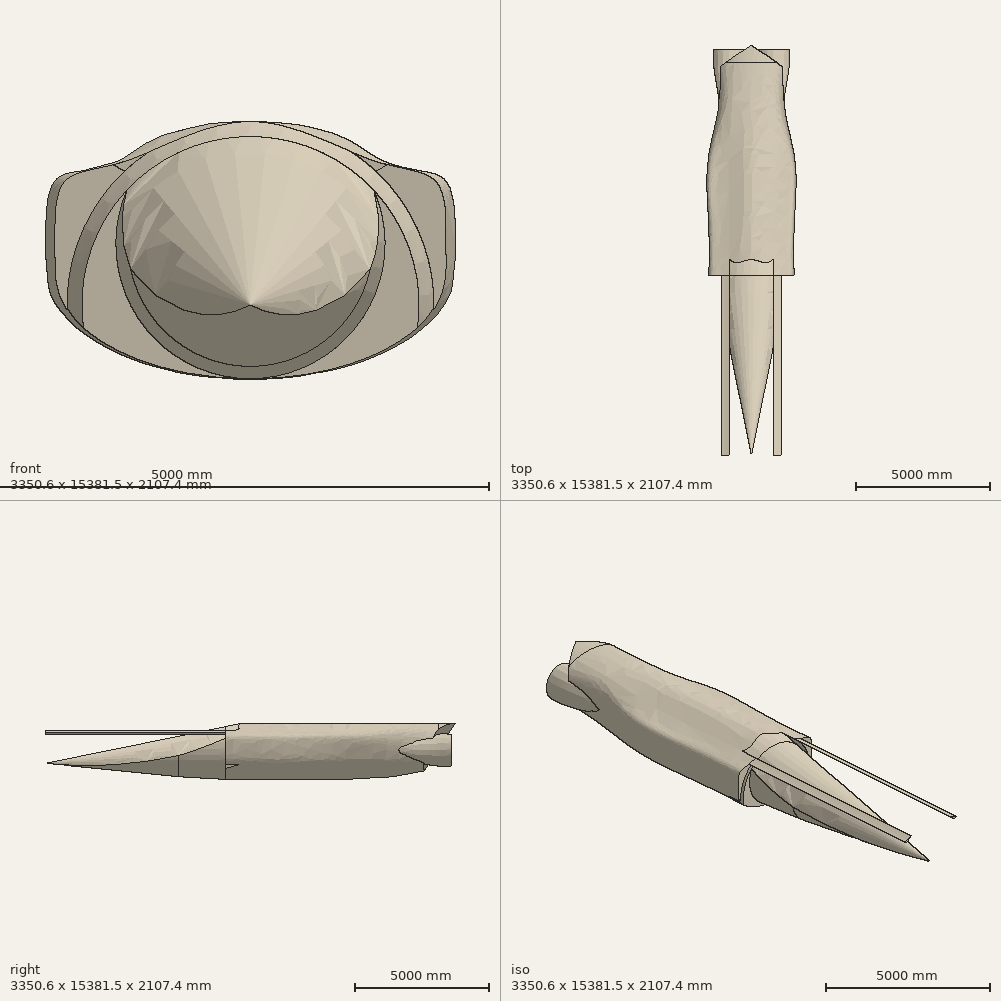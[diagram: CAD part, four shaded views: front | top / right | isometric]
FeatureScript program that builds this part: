
annotation { "Feature Type Name" : "Feature", "Feature Type Description" : "" }
export const myFeature = defineFeature(function(context is Context, id is Id, definition is map)
    precondition{}
    {
        {
            var Q0;
            Q0=qCreatedBy(makeId("Front.planeOp"),FACE);
            cPlane(context, id + "F0", {"entities" : qUnion([Q0]), "cplaneType" : CPlaneType.OFFSET, "offset" : 1750 * mm, "width" : 152.4 * mm, "height" : 152.4 * mm});
        }
        {
            var Q0;
            Q0=qCreatedBy(id+"F0.planeOp",FACE);
            var sketch = newSketch(context, id + "F1", { "sketchPlane" : qUnion([Q0])});
            skPoint(sketch, "E0.middle", {"position": v(0, 0) * mm});
            skFitSpline(sketch, "E1", {"points": [v(0, 1000) * mm, v(1060, 662.5) * mm, v(1517.6, 506.84) * mm, v(1600, 0) * mm, v(1517.6, -506.84) * mm, v(750, -1000) * mm, v(-750, -1000) * mm, v(-1517.6, -506.84) * mm, v(-1600, 0) * mm, v(-1517.6, 506.84) * mm, v(-1060, 662.5) * mm, v(0, 1000) * mm]});
            skSolve(sketch);
        }
        {
            var Q0;
            Q0=qCreatedBy(makeId("Front.planeOp"),FACE);
            var sketch = newSketch(context, id + "F2", { "sketchPlane" : qUnion([Q0])});
            skPoint(sketch, "E2.middle", {"position": v(0, 0) * mm});
            skFitSpline(sketch, "E3", {"points": [v(0, 1000) * mm, v(1060, 662.5) * mm, v(1517.6, 506.84) * mm, v(1600, 0) * mm, v(1517.6, -506.84) * mm, v(750, -1000) * mm, v(-750, -1000) * mm, v(-1517.6, -506.84) * mm, v(-1600, 0) * mm, v(-1517.6, 506.84) * mm, v(-1060, 662.5) * mm, v(0, 1000) * mm]});
            skSolve(sketch);
        }
        {
            var Q0;
            Q0=qCreatedBy(makeId("Front.planeOp"),FACE);
            cPlane(context, id + "F3", {"entities" : qUnion([Q0]), "cplaneType" : CPlaneType.OFFSET, "offset" : 2800 * mm, "oppositeDirection" : true, "width" : 150 * mm, "height" : 150 * mm});
        }
        {
            var Q0;
            Q0=qCreatedBy(id+"F3.planeOp",FACE);
            var sketch = newSketch(context, id + "F4", { "sketchPlane" : qUnion([Q0])});
            skPoint(sketch, "E4.middle", {"position": v(0, 0) * mm});
            skFitSpline(sketch, "E5", {"points": [v(0, 1000) * mm, v(1060, 662.5) * mm, v(1517.6, 506.84) * mm, v(1600, 0) * mm, v(1517.6, -506.84) * mm, v(750, -1000) * mm, v(-750, -1000) * mm, v(-1517.6, -506.84) * mm, v(-1600, 0) * mm, v(-1517.6, 506.84) * mm, v(-1060, 662.5) * mm, v(0, 1000) * mm]});
            skSolve(sketch);
        }
        {
            var Q0;
            Q0=qCreatedBy(makeId("Front.planeOp"),FACE);
            cPlane(context, id + "F5", {"entities" : qUnion([Q0]), "cplaneType" : CPlaneType.OFFSET, "offset" : 4500 * mm, "oppositeDirection" : true, "width" : 150 * mm, "height" : 150 * mm});
        }
        {
            var Q0;
            Q0=qCreatedBy(id+"F5.planeOp",FACE);
            var sketch = newSketch(context, id + "F6", { "sketchPlane" : qUnion([Q0])});
            skPoint(sketch, "E6.middle", {"position": v(0, 0) * mm});
            skFitSpline(sketch, "E7", {"points": [v(0, 1000) * mm, v(1060, 662.5) * mm, v(1250, 0) * mm, v(1060, -662.5) * mm, v(0, -1000) * mm, v(-1060, -662.5) * mm, v(-1250, 0) * mm, v(-1060, 662.5) * mm, v(0, 1000) * mm]});
            skSolve(sketch);
        }
        {
            var Q0;
            Q0=qCreatedBy(makeId("Front.planeOp"),FACE);
            cPlane(context, id + "F7", {"entities" : qUnion([Q0]), "cplaneType" : CPlaneType.OFFSET, "offset" : 6232.05 * mm, "oppositeDirection" : true, "width" : 150 * mm, "height" : 150 * mm});
        }
        {
            var Q0;
            Q0=qCreatedBy(id+"F7.planeOp",FACE);
            var sketch = newSketch(context, id + "F8", { "sketchPlane" : qUnion([Q0])});
            skPoint(sketch, "E8.middle", {"position": v(0, 0) * mm});
            skFitSpline(sketch, "E9", {"points": [v(0, 1000) * mm, v(1060, 662.5) * mm, v(1250, 0) * mm, v(848, -530) * mm, v(-848, -530) * mm, v(-1250, 0) * mm, v(-1060, 662.5) * mm, v(0, 1000) * mm]});
            skSolve(sketch);
        }
        {
            var Q0;
            Q0=qSketchRegion(id+"F1",true);
            var Q1;
            Q1=qSketchRegion(id+"F2",true);
            var Q2;
            Q2=qSketchRegion(id+"F4",true);
            var Q3;
            Q3=qSketchRegion(id+"F6",true);
            var Q4;
            Q4=qSketchRegion(id+"F8",true);
            loft(context, id + "F9", {"sheetProfilesArray" : [{ "sheetProfileEntities" : qUnion([Q0]) }, { "sheetProfileEntities" : qUnion([Q1]) }, { "sheetProfileEntities" : qUnion([Q2]) }, { "sheetProfileEntities" : qUnion([Q3]) }, { "sheetProfileEntities" : qUnion([Q4]) }]});
        }
        {
            var Q0;
            Q0=makeQuery(id+"F9.opLoft","CAP_FACE",FACE,{"disambiguationData":[OSD([makeQuery(id+"F8.imprint","IMPRINT",FACE,{"disambiguationData":[TD([[makeQuery(id+"F8.imprint","IMPRINT",EDGE,{"derivedFrom":sQuery(id+"F8.wireOp",EDGE,"E9")}),-1.0]])]})])],"isStart":true});
            extrude(context, id + "F10", {"entities" : qUnion([Q0]), "operationType" : NewBodyOperationType.ADD, "depth" : 649.4 * mm});
        }
        {
            var Q0;
            Q0=qCreatedBy(makeId("Right.planeOp"),FACE);
            var sketch = newSketch(context, id + "F11", { "sketchPlane" : qUnion([Q0])});
            skLineSegment(sketch, "E10", {"start": v(0, 0) * mm, "end": v(4500, 0) * mm});
            skLineSegment(sketch, "E11", {"start": v(4500, 0) * mm, "end": v(6232.05, 0) * mm});
            skLineSegment(sketch, "E12", {"start": v(4500, 0) * mm, "end": v(4500, 1000) * mm});
            skLineSegment(sketch, "E13", {"start": v(4500, 1000) * mm, "end": v(6881.46, 1000) * mm});
            skLineSegment(sketch, "E14", {"start": v(6881.46, 1000) * mm, "end": v(6881.46, -1000) * mm});
            skLineSegment(sketch, "E15", {"start": v(6881.46, 1000) * mm, "end": v(6232.05, 0) * mm});
            skLineSegment(sketch, "E16", {"start": v(6232.05, 0) * mm, "end": v(5582.64, -1000) * mm});
            skLineSegment(sketch, "E17", {"start": v(5582.64, -1000) * mm, "end": v(6881.46, -1000) * mm});
            skSolve(sketch);
        }
        {
            var Q0;
            Q0=makeQuery(id+"F11.imprint","IMPRINT",FACE,{"disambiguationData":[TD([[makeQuery(id+"F11.imprint","IMPRINT",EDGE,{"derivedFrom":sQuery(id+"F11.wireOp",EDGE,"E14")}),-1.0]])]});
            var Q1;
            Q1=sQuery(id+"F11.wireOp",EDGE,"E13");
            revolve(context, id + "F12", {"operationType" : NewBodyOperationType.REMOVE, "entities" : qUnion([Q0]), "axis" : qUnion([Q1]), "revolveType" : RevolveType.SYMMETRIC, "oppositeDirection" : true, "angle" : 182 * degree});
        }
        {
            var Q0;
            Q0=makeQuery(id+"F9.opLoft","CAP_FACE",FACE,{"disambiguationData":[OSD([makeQuery(id+"F1.imprint","IMPRINT",FACE,{"disambiguationData":[TD([[makeQuery(id+"F1.imprint","IMPRINT",EDGE,{"derivedFrom":sQuery(id+"F1.wireOp",EDGE,"E1")}),-1.0]])]})])],"isStart":true});
            extrude(context, id + "F13", {"entities" : qUnion([Q0]), "depth" : 6750 * mm});
        }
        {
            var Q0;
            Q0=qCreatedBy(makeId("Right.planeOp"),FACE);
            var sketch = newSketch(context, id + "F14", { "sketchPlane" : qUnion([Q0])});
            skLineSegment(sketch, "E18", {"start": v(0, 0) * mm, "end": v(-3500, 0) * mm});
            skLineSegment(sketch, "E19", {"start": v(-3500, 0) * mm, "end": v(-3500, -1000) * mm});
            skLineSegment(sketch, "E20", {"start": v(-3500, -1000) * mm, "end": v(-8500, -1000) * mm});
            skLineSegment(sketch, "E21", {"start": v(-8500, -1000) * mm, "end": v(-8500, -499.31) * mm});
            skLineSegment(sketch, "E22", {"start": v(-1151.4, 0) * mm, "end": v(-1151.4, 1000) * mm});
            skLineSegment(sketch, "E23", {"start": v(-1151.4, 1000) * mm, "end": v(-8500, -499.31) * mm});
            skLineSegment(sketch, "E24", {"start": v(-8500, -499.31) * mm, "end": v(-3500, -1000) * mm});
            skLineSegment(sketch, "E25", {"start": v(-1151.4, 1000) * mm, "end": v(-8500, 1000) * mm});
            skLineSegment(sketch, "E26", {"start": v(-8500, 1000) * mm, "end": v(-8500, -499.31) * mm});
            skLineSegment(sketch, "E27", {"start": v(-8500, -1000) * mm, "end": v(-8500, -1750) * mm});
            skLineSegment(sketch, "E28", {"start": v(-8500, -1750) * mm, "end": v(-1750, -1750) * mm});
            skPoint(sketch, "E28.endSnap0", {"position": v(-1750, 0) * mm});
            skLineSegment(sketch, "E29", {"start": v(-1750, 0) * mm, "end": v(-1750, -1099.92) * mm});
            skLineSegment(sketch, "E30", {"start": v(-1750, -1099.92) * mm, "end": v(-3500, -1000) * mm});
            skLineSegment(sketch, "E31", {"start": v(-1750, -1099.92) * mm, "end": v(-1750, -1750) * mm});
            skLineSegment(sketch, "E32", {"start": v(-8500, -499.31) * mm, "end": v(-3500, -499.31) * mm});
            skSolve(sketch);
        }
        {
            var Q0;
            Q0=makeQuery(id+"F14.imprint","IMPRINT",FACE,{"disambiguationData":[TD([[makeQuery(id+"F14.imprint","IMPRINT",EDGE,{"derivedFrom":sQuery(id+"F14.wireOp",EDGE,"E23")}),-1.0]])]});
            var Q1;
            Q1=sQuery(id+"F14.wireOp",EDGE,"E32");
            revolve(context, id + "F15", {"operationType" : NewBodyOperationType.REMOVE, "entities" : qUnion([Q0]), "axis" : qUnion([Q1]), "revolveType" : RevolveType.SYMMETRIC, "oppositeDirection" : true, "angle" : 250 * degree});
        }
        {
            var Q0;
            Q0=makeQuery(id+"F14.imprint","IMPRINT",FACE,{"disambiguationData":[TD([[makeQuery(id+"F14.imprint","IMPRINT",EDGE,{"derivedFrom":sQuery(id+"F14.wireOp",EDGE,"E20")}),-1.0]])]});
            var Q1;
            Q1=makeQuery(id+"F14.imprint","IMPRINT",FACE,{"disambiguationData":[TD([[makeQuery(id+"F14.imprint","IMPRINT",EDGE,{"derivedFrom":sQuery(id+"F14.wireOp",EDGE,"E20")}),1.0]])]});
            var Q2;
            Q2=sQuery(id+"F14.wireOp",EDGE,"E18");
            revolve(context, id + "F16", {"operationType" : NewBodyOperationType.REMOVE, "entities" : qUnion([Q0, Q1]), "axis" : qUnion([Q2]), "revolveType" : RevolveType.SYMMETRIC, "oppositeDirection" : true, "angle" : 240 * degree});
        }
        {
            var Q0;
            Q0=qCreatedBy(makeId("Front.planeOp"),FACE);
            cPlane(context, id + "F17", {"entities" : qUnion([Q0]), "cplaneType" : CPlaneType.OFFSET, "offset" : 3500 * mm, "oppositeDirection" : true, "width" : 150 * mm, "height" : 150 * mm});
        }
        {
            var Q0;
            Q0=qCreatedBy(id+"F17.planeOp",FACE);
            var sketch = newSketch(context, id + "F18", { "sketchPlane" : qUnion([Q0])});
            skCircle(sketch, "E33", {"center": v(-825, 0) * mm, "radius": 600 * mm});
            skCircle(sketch, "E34", {"center": v(825, 0) * mm, "radius": 600 * mm});
            skSolve(sketch);
        }
        {
            var Q0;
            Q0=qCreatedBy(makeId("Front.planeOp"),FACE);
            cPlane(context, id + "F19", {"entities" : qUnion([Q0]), "cplaneType" : CPlaneType.OFFSET, "offset" : 4500 * mm, "oppositeDirection" : true, "width" : 150 * mm, "height" : 150 * mm});
        }
        {
            var Q0;
            Q0=qCreatedBy(id+"F19.planeOp",FACE);
            var sketch = newSketch(context, id + "F20", { "sketchPlane" : qUnion([Q0])});
            skCircle(sketch, "E35", {"center": v(-825, 0) * mm, "radius": 400 * mm});
            skCircle(sketch, "E36", {"center": v(825, 0) * mm, "radius": 400 * mm});
            skSolve(sketch);
        }
        {
            var Q0;
            Q0=qCreatedBy(makeId("Front.planeOp"),FACE);
            cPlane(context, id + "F21", {"entities" : qUnion([Q0]), "cplaneType" : CPlaneType.OFFSET, "offset" : 6232.05 * mm, "oppositeDirection" : true, "width" : 150 * mm, "height" : 150 * mm});
        }
        {
            var Q0;
            Q0=qCreatedBy(id+"F21.planeOp",FACE);
            var sketch = newSketch(context, id + "F22", { "sketchPlane" : qUnion([Q0])});
            skCircle(sketch, "E37", {"center": v(-825, 0) * mm, "radius": 600 * mm});
            skCircle(sketch, "E38", {"center": v(825, 0) * mm, "radius": 600 * mm});
            skSolve(sketch);
        }
        {
            var Q0;
            Q0=qCreatedBy(makeId("Front.planeOp"),FACE);
            cPlane(context, id + "F23", {"entities" : qUnion([Q0]), "cplaneType" : CPlaneType.OFFSET, "offset" : 6732.05 * mm, "oppositeDirection" : true, "width" : 150 * mm, "height" : 150 * mm});
        }
        {
            var Q0;
            Q0=qCreatedBy(id+"F23.planeOp",FACE);
            var sketch = newSketch(context, id + "F24", { "sketchPlane" : qUnion([Q0])});
            skCircle(sketch, "E39", {"center": v(-825, 0) * mm, "radius": 600 * mm});
            skCircle(sketch, "E40", {"center": v(825, 0) * mm, "radius": 600 * mm});
            skSolve(sketch);
        }
        {
            var Q0;
            Q0=makeQuery(id+"F18.imprint","IMPRINT",FACE,{"disambiguationData":[TD([[makeQuery(id+"F18.imprint","IMPRINT",EDGE,{"derivedFrom":sQuery(id+"F18.wireOp",EDGE,"E33")}),1.0]])]});
            var Q1;
            Q1=makeQuery(id+"F20.imprint","IMPRINT",FACE,{"disambiguationData":[TD([[makeQuery(id+"F20.imprint","IMPRINT",EDGE,{"derivedFrom":sQuery(id+"F20.wireOp",EDGE,"E35")}),1.0]])]});
            var Q2;
            Q2=makeQuery(id+"F22.imprint","IMPRINT",FACE,{"disambiguationData":[TD([[makeQuery(id+"F22.imprint","IMPRINT",EDGE,{"derivedFrom":sQuery(id+"F22.wireOp",EDGE,"E37")}),1.0]])]});
            var Q3;
            Q3=makeQuery(id+"F24.imprint","IMPRINT",FACE,{"disambiguationData":[TD([[makeQuery(id+"F24.imprint","IMPRINT",EDGE,{"derivedFrom":sQuery(id+"F24.wireOp",EDGE,"E39")}),1.0]])]});
            loft(context, id + "F25", {"sheetProfilesArray" : [{ "sheetProfileEntities" : qUnion([Q0]) }, { "sheetProfileEntities" : qUnion([Q1]) }, { "sheetProfileEntities" : qUnion([Q2]) }, { "sheetProfileEntities" : qUnion([Q3]) }]});
        }
        {
            var Q0;
            Q0=makeQuery(id+"F18.imprint","IMPRINT",FACE,{"disambiguationData":[TD([[makeQuery(id+"F18.imprint","IMPRINT",EDGE,{"derivedFrom":sQuery(id+"F18.wireOp",EDGE,"E34")}),1.0]])]});
            var Q1;
            Q1=makeQuery(id+"F20.imprint","IMPRINT",FACE,{"disambiguationData":[TD([[makeQuery(id+"F20.imprint","IMPRINT",EDGE,{"derivedFrom":sQuery(id+"F20.wireOp",EDGE,"E36")}),1.0]])]});
            var Q2;
            Q2=makeQuery(id+"F22.imprint","IMPRINT",FACE,{"disambiguationData":[TD([[makeQuery(id+"F22.imprint","IMPRINT",EDGE,{"derivedFrom":sQuery(id+"F22.wireOp",EDGE,"E38")}),1.0]])]});
            var Q3;
            Q3=makeQuery(id+"F24.imprint","IMPRINT",FACE,{"disambiguationData":[TD([[makeQuery(id+"F24.imprint","IMPRINT",EDGE,{"derivedFrom":sQuery(id+"F24.wireOp",EDGE,"E40")}),1.0]])]});
            loft(context, id + "F26", {"sheetProfilesArray" : [{ "sheetProfileEntities" : qUnion([Q0]) }, { "sheetProfileEntities" : qUnion([Q1]) }, { "sheetProfileEntities" : qUnion([Q2]) }, { "sheetProfileEntities" : qUnion([Q3]) }]});
        }
    });
